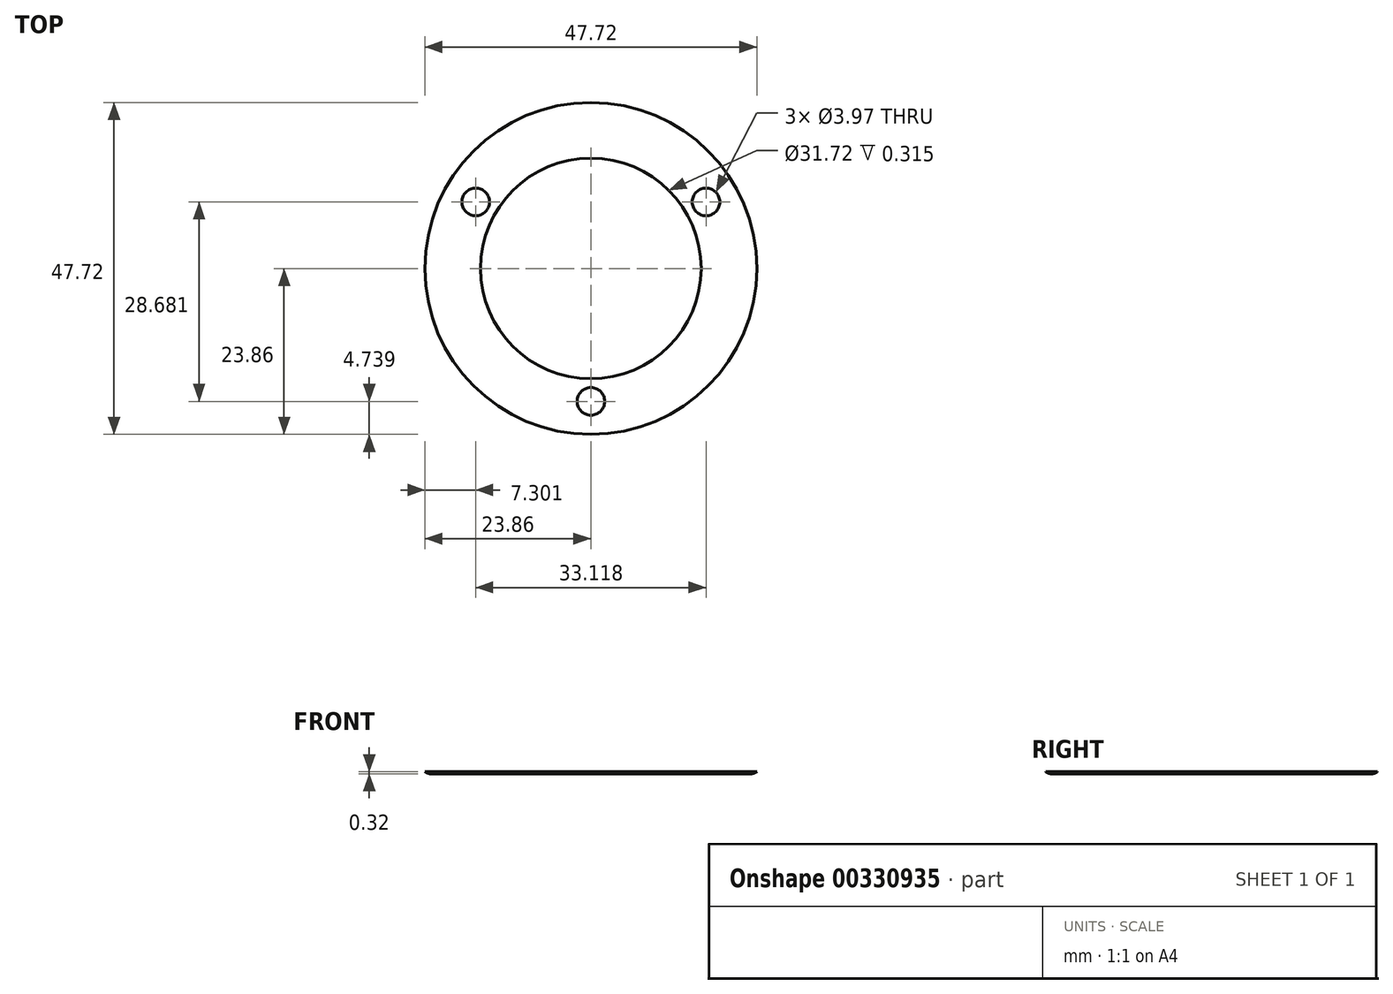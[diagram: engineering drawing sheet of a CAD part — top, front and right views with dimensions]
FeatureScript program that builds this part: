
annotation { "Feature Type Name" : "Feature", "Feature Type Description" : "" }
export const myFeature = defineFeature(function(context is Context, id is Id, definition is map)
    precondition{}
    {
        {
            assignVariable(context, id + "F0", {"name" : "y", "anyValue" : .315});
        }
        {
            var Q0;
            Q0=qCreatedBy(makeId("Top.planeOp"),FACE);
            var sketch = newSketch(context, id + "F1", { "sketchPlane" : qUnion([Q0])});
            skCircle(sketch, "E0", {"center": v(0, 0) * mm, "radius": 23.86 * mm});
            skCircle(sketch, "E1", {"center": v(0, 0) * mm, "radius": 14.34 * mm});
            skCircle(sketch, "E2", {"center": v(0, -19.12) * mm, "radius": 1.98 * mm});
            skCircle(sketch, "E3.1.0", {"center": v(16.56, 9.56) * mm, "radius": 1.98 * mm});
            skCircle(sketch, "E3.2.0", {"center": v(-16.56, 9.56) * mm, "radius": 1.98 * mm});
            skSolve(sketch);
        }
        {
            var Q0;
            Q0 = qSketchRegion(id + "F1", true);
            extrude(context, id + "F2", {"entities" : qUnion([Q0]), "depth" : (getVariable(context, 'y')) * mm});
        }
        {
            var Q0;
            Q0=qCreatedBy(makeId("Front.planeOp"),FACE);
            var sketch = newSketch(context, id + "F3", { "sketchPlane" : qUnion([Q0])});
            skPoint(sketch, "E4", {"position": v(0, 4) * mm});
            skCircle(sketch, "E5", {"center": v(0, 4) * mm, "radius": 1.73 * mm});
            skSolve(sketch);
        }
        {
            var Q0;
            Q0=makeQuery(id+"F3.imprint","IMPRINT",FACE,{"disambiguationData":[TD([[makeQuery(id+"F3.imprint","IMPRINT",EDGE,{"derivedFrom":sQuery(id+"F3.wireOp",EDGE,"E5")}),1.0]])]});
            var Q1;
            Q1=sQuery(id+"F3.wireOp",EDGE,"E5");
            var Q2;
            Q2=makeQuery(id+"F2.opExtrude","SWEPT_FACE",FACE,{"disambiguationData":[OSD([sQuery(id+"F1.wireOp",EDGE,"E0")])]});
            extrude(context, id + "F4", {"entities" : qUnion([Q0]), "operationType" : NewBodyOperationType.REMOVE, "surfaceEntities" : qUnion([Q1]), "endBound" : BoundingType.UP_TO_SURFACE, "oppositeDirection" : true, "endBoundEntityFace" : qUnion([Q2]), "depth" : 25.4 * mm});
        }
        {
            var Q0;
            Q0=makeQuery(id+"F2.opExtrude","CAP_EDGE",EDGE,{"disambiguationData":[OSD([sQuery(id+"F1.wireOp",EDGE,"E0")])],"isStart":true});
            fillet(context, id + "F5", {"entities" : qUnion([Q0]), "radius" : 1.59 * mm, "tangentPropagation" : true, "allowEdgeOverflow" : false});
        }
        {
            var Q0;
            Q0=makeQuery(id+"F2.opExtrude","CAP_FACE",FACE,{"disambiguationData":[OSD([sQuery(id+"F1.wireOp",EDGE,"E0"),sQuery(id+"F1.wireOp",EDGE,"E1"),sQuery(id+"F1.wireOp",EDGE,"E2"),sQuery(id+"F1.wireOp",EDGE,"E3.1.0"),sQuery(id+"F1.wireOp",EDGE,"E3.2.0")])],"isStart":false});
            var sketch = newSketch(context, id + "F6", { "sketchPlane" : qUnion([Q0])});
            skCircle(sketch, "E6", {"center": v(0, 0) * mm, "radius": 15.86 * mm});
            skSolve(sketch);
        }
        {
            var Q0;
            Q0=makeQuery(id+"F6.imprint","IMPRINT",FACE,{"disambiguationData":[TD([[makeQuery(id+"F6.imprint","IMPRINT",EDGE,{"derivedFrom":sQuery(id+"F6.wireOp",EDGE,"E6")}),1.0]])]});
            extrude(context, id + "F7", {"entities" : qUnion([Q0]), "operationType" : NewBodyOperationType.REMOVE, "oppositeDirection" : true, "depth" : 1.78 * mm});
        }
    });
